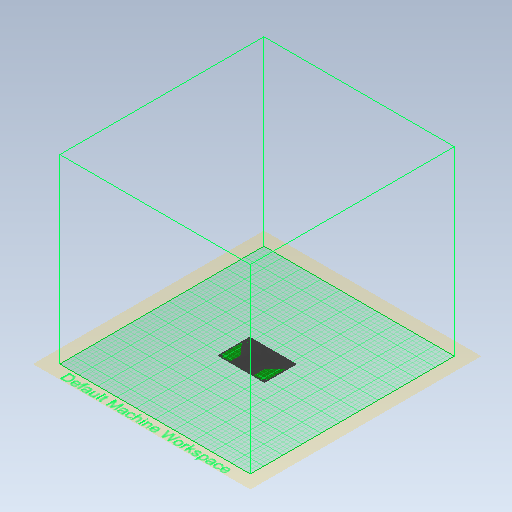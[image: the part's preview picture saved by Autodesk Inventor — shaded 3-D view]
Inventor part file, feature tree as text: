
AUTODESK INVENTOR PART (.ipt)
format: ipt  version: 2021 (Build 250183000, 183)  size: 5,947,392 bytes
history: native  units: in
note: dims shown in document units (in); Inventor stores cm internally (conversion verified against a paired STEP export)
features: sketch x13, extrude x10, projected_geometry x9, pattern_linear x7, mirror x5, hole x1
ambient origin geometry x8: Origin, YZ Plane, XZ Plane, XY Plane, X Axis, Y Axis, Z Axis, Center Point
bodies: Solid1 (feature_tree)
feature tree (45):
  extrude  "Extrusion1"  Depth=2.7in
  hole  "Hole1"  [1 undecoded]
  mirror  "Mirror3"
  sketch  "Sketch9"  dims[d42=0.1in d43=0.11in]
  extrude  "Extrusion5"  Depth=0.11in
  pattern_linear  "Rectangular Pattern6"  Count1=101 Spacing1=0.039in
  extrude  "Extrusion6"  Depth=0.032in TaperAngle=0.0deg
  pattern_linear  "Rectangular Pattern7"  Count1=101 Spacing1=0.039in
  extrude  "Extrusion7"  TaperAngle=0.0deg  [1 undecoded]
  mirror  "Mirror4"
  extrude  "Extrusion9"  Depth=2.0in
  pattern_linear  "Rectangular Pattern9"  Spacing1=0.008in  [1 undecoded]
  sketch  "Sketch16"  dims[d54=1.75in]
  pattern_linear  "Rectangular Pattern10"  Spacing1=1.0in  [1 undecoded]
  extrude  "Extrusion10"  Depth=0.004in TaperAngle=0.0deg
  pattern_linear  "Rectangular Pattern11"  Count1=125 Spacing1=0.016in
  mirror  "Mirror5"
  extrude  "Extrusion11"  Depth=1.0in
  mirror  "Mirror6"
  extrude  "Extrusion12"  Depth=1.0in
  pattern_linear  "Rectangular Pattern12"  Spacing1=0.05in  [1 undecoded]
  extrude  "Extrusion13"  Depth=1.0in
  pattern_linear  "Rectangular Pattern13"  Spacing1=0.0in  [1 undecoded]
  mirror  "Mirror7"
  extrude  "Extrusion14"  Depth=1.0in
  sketch  "Sketch1"  dims[d0=4.0in d1=2.7in]
  sketch  "Sketch7"  dims[d2=0.04in d3=0.0in d41=0.1719in]
  projected_geometry  "Projected Loop6"
  projected_geometry  "Projected Loop8"
  sketch  "Sketch11"  dims[d44=0.17in d45=0.75in d46=0.313in d47=0.164in d48=0.5635in d49=0.12in]
  projected_geometry  "Projected Loop9"
  sketch  "Sketch12"  dims[d50=0.8108in]
  sketch  "Sketch13"  dims[d52=1.5748in]
  sketch  "Sketch15"  dims[d53=0.02in]
  projected_geometry  "Projected Loop11"
  projected_geometry  "Projected Loop12"
  sketch  "Sketch17"  dims[d55=0.0in d56=0.0in d57=39.7638in d59=0.039in]
  projected_geometry  "Projected Loop13"
  sketch  "Sketch18"  dims[d60=0.032in d61=0.0014in d62=0.0in d63=39.7638in d65=0.039in]
  projected_geometry  "Projected Loop14"
  sketch  "Sketch19"  dims[d66=0.0197in d69=0.0in d70=0.0in]
  projected_geometry  "Projected Loop15"
  sketch  "Sketch20"  dims[d71=2.65in d82=2.0in]
  sketch  "Sketch21"  dims[d83=0.25in d84=0.008in d86=1.0in d87=0.004in d88=0.0in d89=49.2126in d91=0.016in d92=39.7638in d94=0.039in d95=0.0198in d96=0.05in d97=0.175in d98=0.0in d99=0.0in d100=5.1181in d102=0.039in d103=0.008in d104=0.008in d105=0.008in d106=0.008in d107=0.008in d108=0.008in d109=0.008in d110=0.008in d111=0.008in d112=0.008in d113=0.008in d114=0.008in d115=0.008in d116=0.008in d117=0.008in d118=0.008in d119=0.008in d120=0.008in d121=0.008in d122=0.008in d123=0.008in d124=0.008in d125=0.008in d126=0.008in d127=0.008in d128=0.008in d129=0.008in d130=0.008in d131=0.008in d132=0.008in d133=0.008in d134=0.008in d135=0.008in d136=0.008in d137=0.008in d138=0.008in d139=0.008in d140=0.008in d141=0.008in d142=0.008in d143=0.008in d144=0.008in d145=0.008in d146=0.008in d147=0.008in d148=0.008in d149=0.008in d150=0.008in d151=0.008in d152=0.008in d153=0.008in d154=0.008in d155=0.008in d156=0.008in d157=0.008in d158=0.008in d159=0.008in d160=0.008in d161=0.008in d162=0.008in d163=0.008in d164=0.008in d165=0.008in d166=0.004in d167=0.0in d168=0.008in d169=0.03in d170=0.004in d171=0.0in d172=5.1181in d174=0.039in d175=0.032in d176=0.004in d177=0.0in d178=39.7638in d180=0.039in d181=1.0in d182=0.0in]
  projected_geometry  "Projected Loop16"
note: 6 required parameter values undecoded (feature->parameter linkage not recoverable at this tier; creation-order binding heuristic only, values carry confidence <= 0.55)
